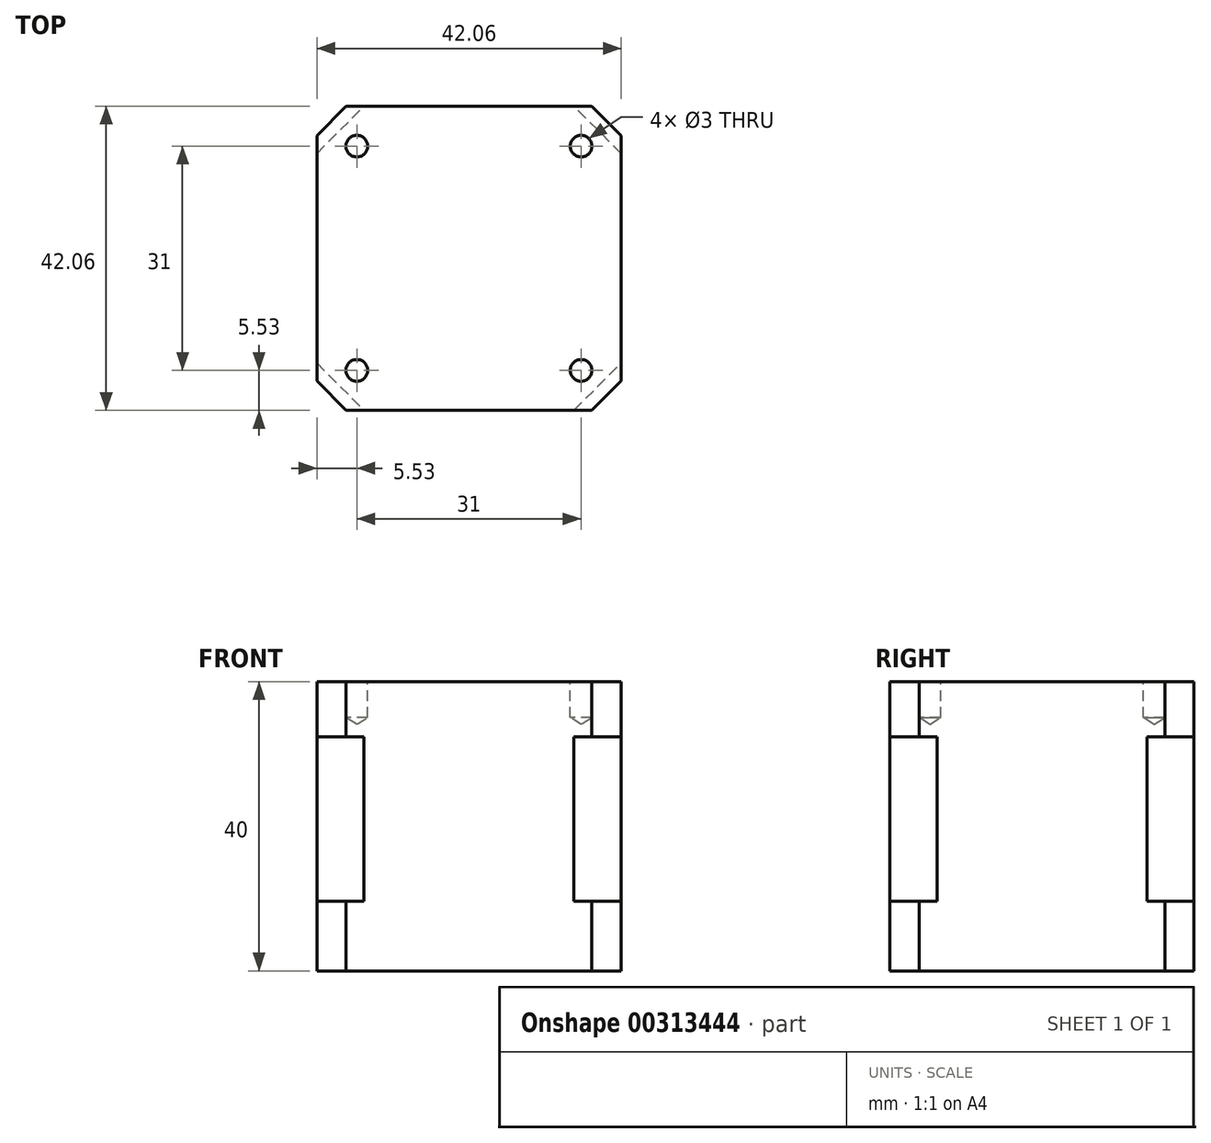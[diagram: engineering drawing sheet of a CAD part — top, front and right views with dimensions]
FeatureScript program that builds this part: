
annotation { "Feature Type Name" : "Feature", "Feature Type Description" : "" }
export const myFeature = defineFeature(function(context is Context, id is Id, definition is map)
    precondition{}
    {
        {
            var Q0;
            Q0=qCreatedBy(makeId("Top.planeOp"),FACE);
            var sketch = newSketch(context, id + "F0", { "sketchPlane" : qUnion([Q0])});
            skLineSegment(sketch, "E0", {"start": v(-16.98, 21.03) * mm, "end": v(16.98, 21.03) * mm});
            skLineSegment(sketch, "E1", {"start": v(16.98, 21.02) * mm, "end": v(21.03, 16.98) * mm});
            skLineSegment(sketch, "E2", {"start": v(21.03, 16.98) * mm, "end": v(21.03, -16.98) * mm});
            skLineSegment(sketch, "E3", {"start": v(21.03, -16.98) * mm, "end": v(16.98, -21.02) * mm});
            skLineSegment(sketch, "E4", {"start": v(16.98, -21.02) * mm, "end": v(-16.98, -21.02) * mm});
            skLineSegment(sketch, "E5", {"start": v(-16.98, -21.02) * mm, "end": v(-21.02, -16.98) * mm});
            skLineSegment(sketch, "E6", {"start": v(-21.02, -16.98) * mm, "end": v(-21.02, 16.98) * mm});
            skLineSegment(sketch, "E7", {"start": v(-21.02, 16.98) * mm, "end": v(-16.98, 21.03) * mm});
            skLineSegment(sketch, "E8", {"start": v(0, 21.02) * mm, "end": v(0, -21.02) * mm, "construction": true});
            skLineSegment(sketch, "E9", {"start": v(21.02, 0) * mm, "end": v(-21.02, 0) * mm, "construction": true});
            skSolve(sketch);
        }
        {
            var Q0;
            Q0 = qSketchRegion(id + "F0", true);
            extrude(context, id + "F1", {"entities" : qUnion([Q0]), "oppositeDirection" : true, "depth" : 40 * mm});
        }
        {
            var Q0;
            Q0=makeQuery(id+"F1.opExtrude","CAP_FACE",FACE,{"disambiguationData":[OSD([sQuery(id+"F0.wireOp",EDGE,"E0"),sQuery(id+"F0.wireOp",EDGE,"E1"),sQuery(id+"F0.wireOp",EDGE,"E2"),sQuery(id+"F0.wireOp",EDGE,"E3"),sQuery(id+"F0.wireOp",EDGE,"E4"),sQuery(id+"F0.wireOp",EDGE,"E5"),sQuery(id+"F0.wireOp",EDGE,"E6"),sQuery(id+"F0.wireOp",EDGE,"E7")])],"isStart":true});
            cPlane(context, id + "F2", {"entities" : qUnion([Q0]), "cplaneType" : CPlaneType.OFFSET, "offset" : 7.65 * mm, "oppositeDirection" : true, "width" : 150 * mm, "height" : 150 * mm});
        }
        {
            var Q0;
            Q0=qCreatedBy(id+"F2.planeOp",FACE);
            var sketch = newSketch(context, id + "F3", { "sketchPlane" : qUnion([Q0])});
            skLineSegment(sketch, "E10", {"start": v(-21.02, 14.5) * mm, "end": v(-14.5, 21.02) * mm});
            skLineSegment(sketch, "E11", {"start": v(-14.5, 21.03) * mm, "end": v(-16.98, 21.03) * mm});
            skLineSegment(sketch, "E12", {"start": v(-16.98, 21.03) * mm, "end": v(-21.02, 16.98) * mm});
            skLineSegment(sketch, "E13", {"start": v(-21.02, 16.98) * mm, "end": v(-21.02, 14.5) * mm});
            skLineSegment(sketch, "E14", {"start": v(14.5, 21.03) * mm, "end": v(16.98, 21.03) * mm});
            skLineSegment(sketch, "E15", {"start": v(16.98, 21.03) * mm, "end": v(21.03, 16.98) * mm});
            skLineSegment(sketch, "E16", {"start": v(21.03, 16.98) * mm, "end": v(21.03, 14.5) * mm});
            skLineSegment(sketch, "E17", {"start": v(21.03, 14.5) * mm, "end": v(14.5, 21.02) * mm});
            skLineSegment(sketch, "E18", {"start": v(14.5, -21.02) * mm, "end": v(21.03, -14.5) * mm});
            skLineSegment(sketch, "E19", {"start": v(21.03, -14.5) * mm, "end": v(21.03, -16.98) * mm});
            skLineSegment(sketch, "E20", {"start": v(21.02, -16.98) * mm, "end": v(16.98, -21.02) * mm});
            skLineSegment(sketch, "E21", {"start": v(16.98, -21.02) * mm, "end": v(14.5, -21.02) * mm});
            skLineSegment(sketch, "E22", {"start": v(-16.98, -21.02) * mm, "end": v(-21.02, -16.98) * mm});
            skLineSegment(sketch, "E23", {"start": v(-21.02, -16.98) * mm, "end": v(-21.02, -14.5) * mm});
            skLineSegment(sketch, "E24", {"start": v(-21.02, -14.5) * mm, "end": v(-14.5, -21.02) * mm});
            skLineSegment(sketch, "E25", {"start": v(-14.5, -21.02) * mm, "end": v(-16.98, -21.02) * mm});
            skLineSegment(sketch, "E26", {"start": v(-17.77, 17.77) * mm, "end": v(17.77, -17.77) * mm, "construction": true});
            skLineSegment(sketch, "E27", {"start": v(17.77, 17.77) * mm, "end": v(-17.77, -17.77) * mm, "construction": true});
            skPoint(sketch, "E28", {"position": v(0, 0) * mm});
            skSolve(sketch);
        }
        {
            var Q0;
            Q0 = qSketchRegion(id + "F3", true);
            var Q1;
            Q1=makeQuery(id+"F1.opExtrude","CAP_FACE",FACE,{"disambiguationData":[OSD([sQuery(id+"F0.wireOp",EDGE,"E0"),sQuery(id+"F0.wireOp",EDGE,"E1"),sQuery(id+"F0.wireOp",EDGE,"E2"),sQuery(id+"F0.wireOp",EDGE,"E3"),sQuery(id+"F0.wireOp",EDGE,"E4"),sQuery(id+"F0.wireOp",EDGE,"E5"),sQuery(id+"F0.wireOp",EDGE,"E6"),sQuery(id+"F0.wireOp",EDGE,"E7")])],"isStart":false});
            extrude(context, id + "F4", {"entities" : qUnion([Q0, Q1]), "operationType" : NewBodyOperationType.REMOVE, "oppositeDirection" : true, "depth" : 22.7 * mm});
        }
        {
            var Q0;
            Q0=makeQuery(id+"F1.opExtrude","CAP_FACE",FACE,{"disambiguationData":[OSD([sQuery(id+"F0.wireOp",EDGE,"E0"),sQuery(id+"F0.wireOp",EDGE,"E1"),sQuery(id+"F0.wireOp",EDGE,"E2"),sQuery(id+"F0.wireOp",EDGE,"E3"),sQuery(id+"F0.wireOp",EDGE,"E4"),sQuery(id+"F0.wireOp",EDGE,"E5"),sQuery(id+"F0.wireOp",EDGE,"E6"),sQuery(id+"F0.wireOp",EDGE,"E7")])],"isStart":true});
            var sketch = newSketch(context, id + "F5", { "sketchPlane" : qUnion([Q0])});
            skPoint(sketch, "E29", {"position": v(-15.5, 15.5) * mm});
            skLineSegment(sketch, "E30.bottom", {"start": v(-15.5, 15.5) * mm, "end": v(15.5, 15.5) * mm});
            skLineSegment(sketch, "E30.top", {"start": v(-15.5, -15.5) * mm, "end": v(15.5, -15.5) * mm});
            skLineSegment(sketch, "E30.left", {"start": v(-15.5, 15.5) * mm, "end": v(-15.5, -15.5) * mm});
            skLineSegment(sketch, "E30.right", {"start": v(15.5, 15.5) * mm, "end": v(15.5, -15.5) * mm});
            skPoint(sketch, "E30.middle", {"position": v(0, 0) * mm});
            skPoint(sketch, "E31", {"position": v(15.5, 15.5) * mm});
            skPoint(sketch, "E32", {"position": v(15.5, -15.5) * mm});
            skPoint(sketch, "E33", {"position": v(-15.5, -15.5) * mm});
            skSolve(sketch);
        }
        {
            var Q0;
            Q0=sQuery(id+"F5.wireOp",VERTEX,"E29");
            var Q1;
            Q1=sQuery(id+"F5.wireOp",VERTEX,"E31");
            var Q2;
            Q2=sQuery(id+"F5.wireOp",VERTEX,"E32");
            var Q3;
            Q3=sQuery(id+"F5.wireOp",VERTEX,"E33");
            var Q4;
            Q4=makeQuery(id+"F1.opExtrude","SWEPT_BODY",BODY,{"disambiguationData":[OSD([sQuery(id+"F0.wireOp",EDGE,"E0"),sQuery(id+"F0.wireOp",EDGE,"E1"),sQuery(id+"F0.wireOp",EDGE,"E2"),sQuery(id+"F0.wireOp",EDGE,"E3"),sQuery(id+"F0.wireOp",EDGE,"E4"),sQuery(id+"F0.wireOp",EDGE,"E5"),sQuery(id+"F0.wireOp",EDGE,"E6"),sQuery(id+"F0.wireOp",EDGE,"E7")])]});
            hole(context, id + "F6", {"style" : HoleStyle.SIMPLE, "endStyle" : HoleEndStyle.BLIND, "holeDiameter" : 3 * mm, "holeDepth" : 5 * mm, "tappedDepth" : 12 * mm, "tapClearance" : 3, "locations" : qUnion([Q0, Q1, Q2, Q3]), "scope" : qUnion([Q4])});
        }
    });
